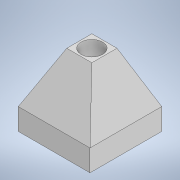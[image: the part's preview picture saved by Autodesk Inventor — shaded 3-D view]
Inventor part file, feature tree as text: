
AUTODESK INVENTOR PART (.ipt)
format: ipt  version: 2020 (Build 240168000, 168)  size: 124,416 bytes
history: native  units: in
note: dims shown in document units (in); Inventor stores cm internally (conversion verified against a paired STEP export)
features: extrude x4, sketch x4
ambient origin geometry x8: Origin, YZ Plane, XZ Plane, XY Plane, X Axis, Y Axis, Z Axis, Center Point
bodies: Solid1 (feature_tree)
feature tree (8):
  extrude  "Extrusion1"  Depth=0.3937in
  extrude  "Extrusion2"  Depth=0.3937in
  extrude  "Extrusion3"  Depth=0.2756in
  extrude  "Extrusion4"  Depth=0.3937in
  sketch  "Sketch3"  dims[d0=0.3937in d1=0.3937in]
  sketch  "Sketch4"  dims[d2=0.3937in d3=0.0in d4=0.1378in]
  sketch  "Sketch6"  dims[d5=0.2756in d6=0.2756in]
  sketch  "Sketch7"  dims[d7=0.3937in d8=0.0in d12=0.1378in d13=0.2756in d14=0.2756in d15=0.3937in d16=0.0in d17=0.0689in d18=0.1181in d19=0.3937in d20=0.0in]
